# Revit family: for update_48495CHN_new
name_source: partatom
category: Plumbing Fixtures
revit_build: Autodesk Revit 2018 (Build: 20170223_1515(x64)
units: mm (PartAtom-declared; Revit-internal decimal feet)

## family parameters
Always vertical = No
Cut with Voids When Loaded = No
OmniClass Number = 23.31.17.00
OmniClass Title = Showers
Part Type = Normal
Room Calculation Point = No
Round Connector Dimension = Use Diameter
Shared = No
Work Plane-Based = Yes

## types (3) — shared parameters
Always visible = Yes
BIMobject category = Showers
Connector Description = Water Inlet 12.7mm
Date of publishing = 9/28/2022 12:00:00 AM
Default Elevation = 1219.2 mm  [stored 4 ft]
Description = AXOR One Ceiling connector 300 mm for overhead shower 280 1jet
Diameter = 13 mm
EAN code = 4059625469408
Edition number = 1
IFC Classification = Sanitary Terminal
Manufacturer = AXOR
Manufacturer name = AXOR
Masterformat 2014 Code = 22 41 23
Masterformat 2014 Description = Residential Showers
Model = 48495CHN
OmniClass Code = 23-31 17 00
OmniClass Description = Showers
Product Guid = 6117a5c8-3445-4e9c-b26d-c1e3ca081995
Product SKU = 48495CHN
Product data url = https://bimobject.com
Product family = AXOR One
Product group = Shower arms
Product name = 48495CHN AXOR One Ceiling connector 300 mm for overhead shower 280 1jet
Product url = https://www.axor-design.com
QR code = https://bimobject.com
UNSPSC Code = 30181503
URL = https://www.axor-design.com
Uniclass 2015 Code = Pr_40_20_87_76
Uniclass 2015 Name = Shower heads
Uniformat II Code = D2010
Uniformat II Description = Plumbing Fixtures
Weight Net (Kg) = 1.6

## per-type parameters (varying)
| type | Material 1 |
| 007 Chrome | AXOR - Metal - 007 Chrome |
| 677 Matte Black | AXOR - Metal - 677 Matte Black |
| 707 Matte White | AXOR - Metal - 707 Matte White |

note: [stored X ft] marks values corroborated as IEEE doubles in the binary element streams (Revit-internal decimal feet)

## geometry (parser evidence)
native form markers: Sweep x4
no freeform markers — native parametric forms only
